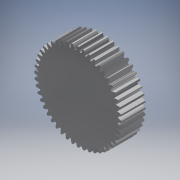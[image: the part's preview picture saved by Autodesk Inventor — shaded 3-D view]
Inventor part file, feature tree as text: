
AUTODESK INVENTOR PART (.ipt)
format: ipt  version: 2019 (Build 230136000, 136)  size: 329,216 bytes
history: native  units: mm (DEFAULTED — no unit token found)
features: plane x3, other x3, sketch x2, extrude x1
ambient origin geometry x8: Origin, YZ Plane, XZ Plane, XY Plane, X Axis, Y Axis, Z Axis, Center Point
bodies: Solid1 (feature_tree)
feature tree (9):
  extrude  "Extrusion1"  Depth=2.75mm TaperAngle=0.0deg
  plane  "Work Plane2"
  plane  "Work Plane8"
  plane  "Work Plane9"
  other  "Spur Gear"
  sketch  "Sketch1"  dims[d0=9.95mm d1=2.75mm d2=0.0mm]
  sketch  "Sketch2"  dims[d3=9.56mm d4=10.0mm d5=0.0mm d16=5.975mm d17=0.0mm d34=0.654498mm d39=0.0mm d41=0.0mm d43=5.975mm d46=5.975mm d47=0.0mm d48=0.0mm]
  other  "Srf1"
  other  "Pitch Diameter"
